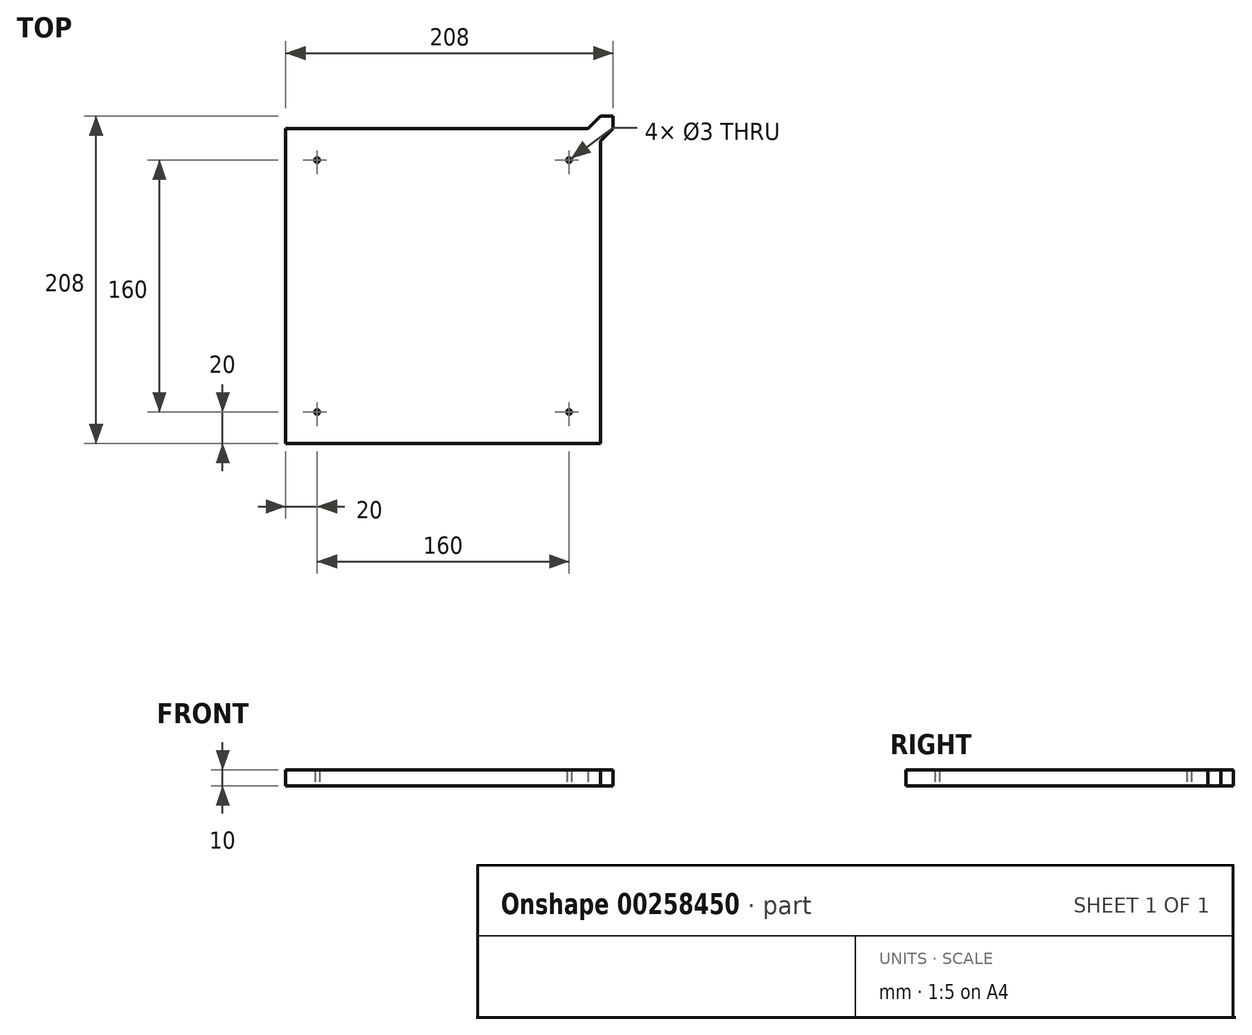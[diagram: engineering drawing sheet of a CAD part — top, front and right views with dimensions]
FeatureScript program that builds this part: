
annotation { "Feature Type Name" : "Feature", "Feature Type Description" : "" }
export const myFeature = defineFeature(function(context is Context, id is Id, definition is map)
    precondition{}
    {
        {
            var Q0;
            Q0=qCreatedBy(makeId("Top.planeOp"),FACE);
            var sketch = newSketch(context, id + "F0", { "sketchPlane" : qUnion([Q0])});
            skLineSegment(sketch, "E0.rect.bottom", {"start": v(92, 92) * mm, "end": v(-92, 92) * mm});
            skLineSegment(sketch, "E0.rect.top", {"start": v(92, -92) * mm, "end": v(-92, -92) * mm});
            skLineSegment(sketch, "E0.rect.left", {"start": v(92, 92) * mm, "end": v(92, -92) * mm});
            skLineSegment(sketch, "E0.rect.right", {"start": v(-92, 92) * mm, "end": v(-92, -92) * mm});
            skPoint(sketch, "E0.rect.middle", {"position": v(0, 0) * mm});
            skLineSegment(sketch, "E1.0", {"start": v(100, 100) * mm, "end": v(-100, 100) * mm});
            skLineSegment(sketch, "E1.1", {"start": v(100, 100) * mm, "end": v(100, -100) * mm});
            skLineSegment(sketch, "E1.2", {"start": v(100, -100) * mm, "end": v(-100, -100) * mm});
            skLineSegment(sketch, "E1.3", {"start": v(-100, 100) * mm, "end": v(-100, -100) * mm});
            skLineSegment(sketch, "E2.rect.bottom", {"start": v(92, 92) * mm, "end": v(100, 92) * mm});
            skLineSegment(sketch, "E2.rect.top", {"start": v(100, 108) * mm, "end": v(108, 108) * mm});
            skLineSegment(sketch, "E2.rect.left", {"start": v(92, 92) * mm, "end": v(92, 100) * mm});
            skPoint(sketch, "E2.rect.middle", {"position": v(100, 100) * mm});
            skLineSegment(sketch, "E3", {"start": v(108, 100) * mm, "end": v(100, 92) * mm});
            skLineSegment(sketch, "E4", {"start": v(100, 108) * mm, "end": v(92, 100) * mm});
            skLineSegment(sketch, "E5", {"start": v(108, 100) * mm, "end": v(108, 108) * mm});
            skPoint(sketch, "E6.end.orphan", {"position": v(108, 92) * mm});
            skPoint(sketch, "E7.orphan", {"position": v(92, 108) * mm});
            skCircle(sketch, "E8", {"center": v(-80, 80) * mm, "radius": 1.5 * mm});
            skCircle(sketch, "E9.MirrorC", {"center": v(80, 80) * mm, "radius": 1.5 * mm});
            skCircle(sketch, "E10.MirrorC", {"center": v(-80, -80) * mm, "radius": 1.5 * mm});
            skCircle(sketch, "E11.MirrorC", {"center": v(80, -80) * mm, "radius": 1.5 * mm});
            skSolve(sketch);
        }
        {
            var Q0;
            Q0=makeQuery(id+"F0.imprint","IMPRINT",FACE,{"disambiguationData":[TD([[makeQuery(id+"F0.imprint","IMPRINT",EDGE,{"derivedFrom":sQuery(id+"F0.wireOp",EDGE,"E0.rect.bottom")}),1.0]])]});
            var Q1;
            Q1=makeQuery(id+"F0.imprint","IMPRINT",FACE,{"disambiguationData":[TD([[makeQuery(id+"F0.imprint","IMPRINT",EDGE,{"derivedFrom":sQuery(id+"F0.wireOp",EDGE,"E0.rect.bottom")}),-1.0]])]});
            var Q2;
            {var subQ4=sQuery(id+"F0.wireOp",EDGE,"E2.rect.bottom");Q2=makeQuery(id+"F0.imprint","IMPRINT",FACE,{"disambiguationData":[TD([[makeQuery(id+"F0.imprint","IMPRINT",EDGE,{"derivedFrom":subQ4}),1.0]])]});}
            var Q3;
            Q3=makeQuery(id+"F0.imprint","IMPRINT",FACE,{"disambiguationData":[TD([[makeQuery(id+"F0.imprint","IMPRINT",EDGE,{"derivedFrom":sQuery(id+"F0.wireOp",EDGE,"E2.rect.top")}),-1.0]])]});
            extrude(context, id + "F1", {"entities" : qUnion([Q0, Q1, Q2, Q3]), "depth" : 10 * mm});
        }
    });
